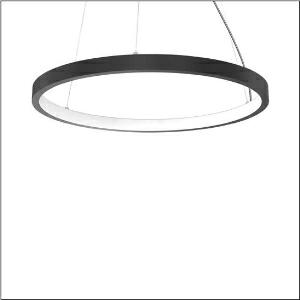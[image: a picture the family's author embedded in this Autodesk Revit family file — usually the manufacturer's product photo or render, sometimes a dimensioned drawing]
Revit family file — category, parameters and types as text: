
# Revit family: silica_r__21_ring-i_5pjbi4d1104a_67cd
name_source: partatom
category: Lighting Fixtures
units: mm (PartAtom-declared; Revit-internal decimal feet)

## family parameters
Cut with Voids When Loaded = No
Host = Face
Light Source = No
Part Type = Normal
Room Calculation Point = No
Round Connector Dimension = Use Diameter
Shared = No

## types (1)
- Silica® 21 Ring-I (1 x LED, 8460 lm, 140 W, 3000K)
    Apparent Load = 140 VA
    CIE Flux Codes = 22 48 76 50 101
    Color Rendering = 80
    Color Temperature = 3000K
    Default Elevation = 1800 mm
    Description = Silica® 21 Ring-I, suspended luminaire, of PMMA, frosted, light emission: inner ring side luminous distribution, primary light characteristic: symmetric, installation type: suspended mounting, LED, rated luminous flux: 8.460lm, luminous efficacy: 61lm/W, light colour: 830, colour temperature: 3000K, with terminal, 5-pole, mains connection: 230V, AC/DC, 0/50..60Hz, rated input power: 140W, housing, of extruded aluminium section, jet black (RAL 9005), diameter: 1.470mm, ceiling canopy, jet black (RAL 9005), protection rating (lamp compartment): IP40, insulation class (complete): insulation class I (protective earthing), certification: CE, impact resistance: IK02, permissible operating ambient temperature: 0..+35°C, packaging unit: 1 piece
    Height = 48 mm  [stored 0.15748 ft]
    Lamp = 1 x LED
    Lamp Light Flux = 8460 lm
    Lamp Power = 140 W
    Lamp count = 1
    Length = 1470 mm
    Luminous efficacy = 60 lm/W
    Manufacturer = Siteco
    ModVariant = No
    Model = 5PJBI4D1104A
    Mounting Place = Ceiling
    Mounting Type = Pendant
    Number of Poles = 1
    OnlyDefault = Yes
    Power Factor = 1
    Product Name = Silica® 21 Ring-I
    Product group = suspended luminaire
    ProductGroupID = 904
    Protection Class = Protection class I
    Protection Degree = IP 40
    RLX_Detail_Level = 1
    RLX_Emergency_Light_Flux = 0 lm
    RLX_Emergency_Type = 0
    RLX_Emergency_Type_DB = No
    RlxData = <blob elided: 20369 chars, md5=409a6785>
    Socket = socket
    Standby Power = 0 W
    System Light Flux = 8460 lm
    System Power = 140 W
    Type Comments = Product without accessories
    Type Image = l_1258373.jpg
    URL = http://relux.com
    VarID = ---
    Voltage = 0 V
    Weight = 0.00 kg
    Width = 0 mm  [stored 0 ft]

note: [stored X ft] marks values corroborated as IEEE doubles in the binary element streams (Revit-internal decimal feet)

## geometry (parser evidence)
native form markers: Blend x4, Sweep x12
no freeform markers — native parametric forms only
